# Revit family: STS-715К Сканер отпечатка пальца_RV17_LOD400 (07.12.23)
name_source: partatom
category: Датчики
revit_build: Autodesk Revit 2017 (Build: 20170118_1100(x64)
units: mm (PartAtom-declared; Revit-internal decimal feet)

## family parameters
Всегда вертикально = Нет
На основе рабочей плоскости = Да
Общий = Нет
При загрузке вырезать с полостями = Нет
Размер круглого соединителя = Использовать диаметр
Сохранять ориентацию аннотаций = Нет
Тип детали = Нормальный
Точка расчета площади = Нет

## types (1)
- STS-715К
    ADSK_URL страницы изделия = https://stilsoft.ru
    ADSK_Единица измерения = шт.
    ADSK_Завод-изготовитель = ООО «Основа Безопасности»
    ADSK_Количество = 1
    ADSK_Марка = CТАЕ.431295.021
    ADSK_Масса = 0.6
    ADSK_Наименование = Сканер отпечатка пальца LAN STS-715К
    d_короба = 20 мм
    Источник освещения = инфракрасный светодиод
    Напряжение = 12
    Отметка по умолчанию = 1219 мм
    Подключение устройств = 1 вход TTL
    Потребляемый ток (без дополнительных внешних потребителей), не более, А = 0 А
    Размер графического файла отпечатка пальца, кБ = 150
    Разрешающая способность изображения, пикс. / dpi = 480x320 / 500
    Скорость коммуникации Ethernet, Мбит/с = 10
    Стандарт интерфейса связи = Ethernet
    Точность распознавания отпечатков пальцев = FAR-10-6, FRR-10-2
    Управление внешними устройствами = 1 выход открытый коллектор до 100мА
